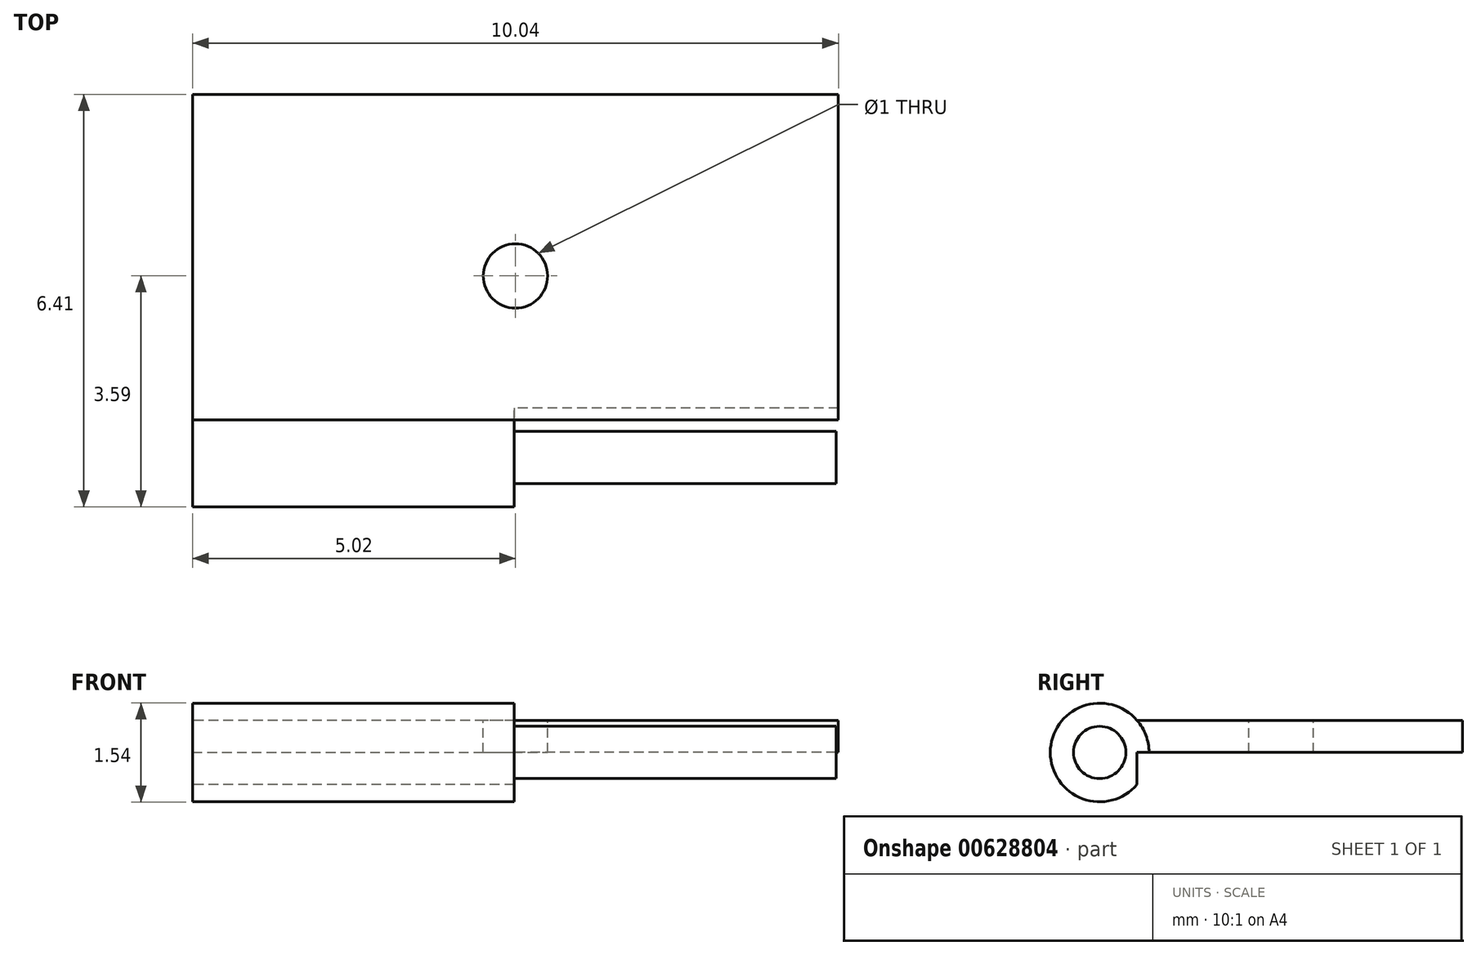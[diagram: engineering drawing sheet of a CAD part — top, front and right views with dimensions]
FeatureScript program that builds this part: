
annotation { "Feature Type Name" : "Feature", "Feature Type Description" : "" }
export const myFeature = defineFeature(function(context is Context, id is Id, definition is map)
    precondition{}
    {
        {
            var Q0;
            Q0=qCreatedBy(makeId("Top.planeOp"),FACE);
            var sketch = newSketch(context, id + "F0", { "sketchPlane" : qUnion([Q0])});
            skLineSegment(sketch, "E0.bottom", {"start": v(5.02, -2.82) * mm, "end": v(-5.02, -2.82) * mm});
            skLineSegment(sketch, "E0.top", {"start": v(5.02, 2.82) * mm, "end": v(-5.02, 2.82) * mm});
            skLineSegment(sketch, "E0.left", {"start": v(5.02, -2.82) * mm, "end": v(5.02, 2.82) * mm});
            skLineSegment(sketch, "E0.right", {"start": v(-5.02, -2.82) * mm, "end": v(-5.02, 2.82) * mm});
            skPoint(sketch, "E0.middle", {"position": v(0, 0) * mm});
            skSolve(sketch);
        }
        {
            var Q0;
            Q0=makeQuery(id+"F0.imprint","IMPRINT",FACE,{"disambiguationData":[TD([[makeQuery(id+"F0.imprint","IMPRINT",EDGE,{"derivedFrom":sQuery(id+"F0.wireOp",EDGE,"E0.bottom")}),-1.0]])]});
            extrude(context, id + "F1", {"entities" : qUnion([Q0]), "depth" : 1 * mm, "offsetDistance" : 25 * mm});
        }
        {
            var Q0;
            Q0=makeQuery(id+"F1.opExtrude","SWEPT_FACE",FACE,{"disambiguationData":[OSD([sQuery(id+"F0.wireOp",EDGE,"E0.right")])]});
            var sketch = newSketch(context, id + "F2", { "sketchPlane" : qUnion([Q0])});
            skCircle(sketch, "E1", {"center": v(2.82, 0.5) * mm, "radius": 0.77 * mm});
            skSolve(sketch);
        }
        {
            var Q0;
            Q0 = qSketchRegion(id + "F2", true);
            extrude(context, id + "F3", {"entities" : qUnion([Q0]), "operationType" : NewBodyOperationType.REMOVE, "oppositeDirection" : true, "depth" : 10.08 * mm, "offsetDistance" : 25 * mm});
        }
        {
            var Q0;
            Q0 = qSketchRegion(id + "F2", true);
            extrude(context, id + "F4", {"entities" : qUnion([Q0]), "operationType" : NewBodyOperationType.ADD, "oppositeDirection" : true, "depth" : 5 * mm, "offsetDistance" : 25 * mm});
        }
        {
            var Q0;
            Q0=makeQuery(id+"F4.boolean.opBoolean","MERGE",FACE,{"derivedFrom":[makeQuery(id+"F1.opExtrude","SWEPT_FACE",FACE,{"disambiguationData":[OSD([sQuery(id+"F0.wireOp",EDGE,"E0.right")])]}),makeQuery(id+"F4.opExtrude","CAP_FACE",FACE,{"disambiguationData":[OSD([sQuery(id+"F2.wireOp",EDGE,"E1")])],"isStart":true})]});
            var sketch = newSketch(context, id + "F5", { "sketchPlane" : qUnion([Q0])});
            skCircle(sketch, "E2", {"center": v(2.82, 0.5) * mm, "radius": 0.4 * mm});
            skSolve(sketch);
        }
        {
            var Q0;
            Q0 = qSketchRegion(id + "F5", true);
            extrude(context, id + "F6", {"entities" : qUnion([Q0]), "operationType" : NewBodyOperationType.ADD, "oppositeDirection" : true, "depth" : 10 * mm, "offsetDistance" : 25 * mm});
        }
        {
            var Q0;
            Q0=makeQuery(id+"F1.opExtrude","CAP_FACE",FACE,{"disambiguationData":[OSD([sQuery(id+"F0.wireOp",EDGE,"E0.bottom"),sQuery(id+"F0.wireOp",EDGE,"E0.top"),sQuery(id+"F0.wireOp",EDGE,"E0.left"),sQuery(id+"F0.wireOp",EDGE,"E0.right")])],"isStart":false});
            var sketch = newSketch(context, id + "F7", { "sketchPlane" : qUnion([Q0])});
            skPoint(sketch, "E3", {"position": v(0, 0) * mm});
            skSolve(sketch);
        }
        {
            var Q0;
            Q0=sQuery(id+"F7.wireOp",VERTEX,"E3");
            var Q1;
            Q1=makeQuery(id+"F1.opExtrude","SWEPT_BODY",BODY,{"disambiguationData":[OSD([sQuery(id+"F0.wireOp",EDGE,"E0.bottom"),sQuery(id+"F0.wireOp",EDGE,"E0.top"),sQuery(id+"F0.wireOp",EDGE,"E0.left"),sQuery(id+"F0.wireOp",EDGE,"E0.right")])]});
            hole(context, id + "F8", {"style" : HoleStyle.SIMPLE, "endStyle" : HoleEndStyle.BLIND, "holeDiameter" : 1 * mm, "majorDiameter" : 5 * mm, "holeDepth" : 2 * mm, "isTappedThrough" : true, "tappedDepth" : 12 * mm, "tapClearance" : 3, "locations" : qUnion([Q0]), "scope" : qUnion([Q1])});
        }
        {
            var Q0;
            Q0=makeQuery(id+"F1.opExtrude","SWEPT_FACE",FACE,{"disambiguationData":[OSD([sQuery(id+"F0.wireOp",EDGE,"E0.left")])]});
            var sketch = newSketch(context, id + "F9", { "sketchPlane" : qUnion([Q0])});
            skLineSegment(sketch, "E4.bottom", {"start": v(-2.24, 0) * mm, "end": v(2.82, 0) * mm});
            skLineSegment(sketch, "E4.top", {"start": v(-2.24, 0.5) * mm, "end": v(2.82, 0.5) * mm});
            skLineSegment(sketch, "E4.left", {"start": v(-2.24, 0) * mm, "end": v(-2.24, 0.5) * mm});
            skLineSegment(sketch, "E4.right", {"start": v(2.82, 0) * mm, "end": v(2.82, 0.5) * mm});
            skSolve(sketch);
        }
        {
            var Q0;
            Q0 = qSketchRegion(id + "F9", true);
            extrude(context, id + "F10", {"entities" : qUnion([Q0]), "operationType" : NewBodyOperationType.REMOVE, "oppositeDirection" : true, "depth" : 25 * mm, "offsetDistance" : 25 * mm});
        }
    });
